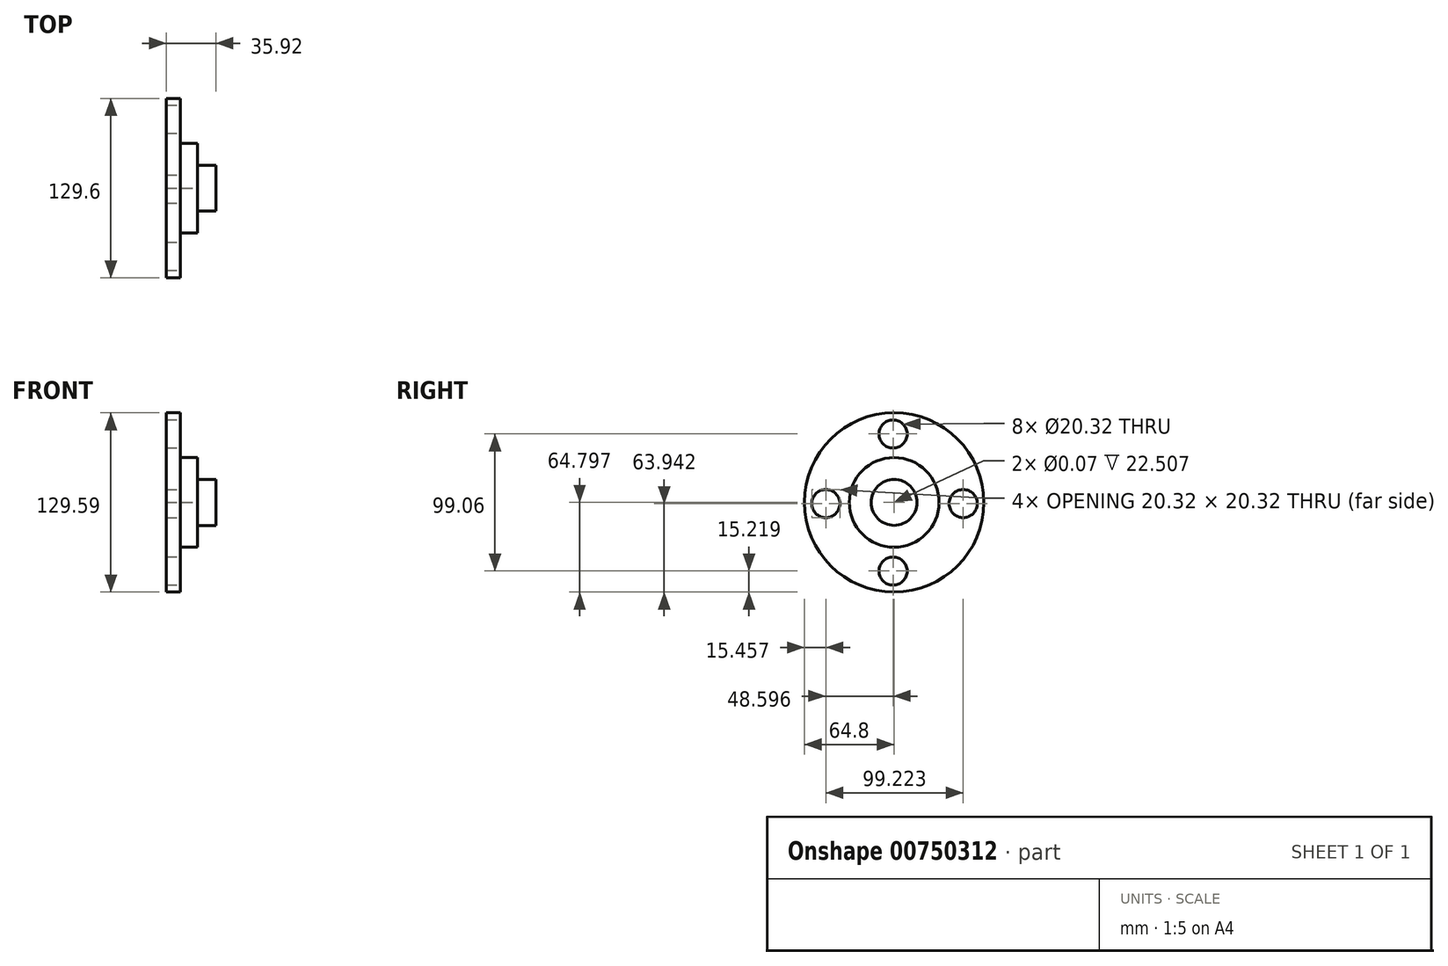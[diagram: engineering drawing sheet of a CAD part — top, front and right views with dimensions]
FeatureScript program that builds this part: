
annotation { "Feature Type Name" : "Feature", "Feature Type Description" : "" }
export const myFeature = defineFeature(function(context is Context, id is Id, definition is map)
    precondition{}
    {
        {
            var Q0;
            Q0=qCreatedBy(makeId("Front.planeOp"),FACE);
            var sketch = newSketch(context, id + "F0", { "sketchPlane" : qUnion([Q0])});
            skLineSegment(sketch, "E0", {"start": v(0, 64.76) * mm, "end": v(0, 0) * mm});
            skLineSegment(sketch, "E1", {"start": v(0, 0) * mm, "end": v(10.3, 0) * mm});
            skLineSegment(sketch, "E2", {"start": v(10.3, 0) * mm, "end": v(10.3, 64.76) * mm});
            skLineSegment(sketch, "E3", {"start": v(10.3, 64.76) * mm, "end": v(0, 64.76) * mm});
            skLineSegment(sketch, "E4", {"start": v(10.3, 0) * mm, "end": v(22.5, 0) * mm});
            skLineSegment(sketch, "E5", {"start": v(22.5, 0) * mm, "end": v(22.5, 32.38) * mm});
            skLineSegment(sketch, "E6", {"start": v(22.5, 32.38) * mm, "end": v(10.3, 32.38) * mm});
            skLineSegment(sketch, "E7", {"start": v(10.3, 32.38) * mm, "end": v(10.3, 0) * mm});
            skLineSegment(sketch, "E8", {"start": v(22.5, 16.55) * mm, "end": v(35.92, 16.55) * mm});
            skLineSegment(sketch, "E9", {"start": v(35.92, 16.55) * mm, "end": v(35.92, -0.03) * mm});
            skLineSegment(sketch, "E10", {"start": v(35.92, -0.03) * mm, "end": v(22.5, -0.03) * mm});
            skLineSegment(sketch, "E11", {"start": v(22.5, -0.03) * mm, "end": v(22.5, 16.55) * mm});
            skSolve(sketch);
        }
        {
            var Q0;
            Q0 = qSketchRegion(id + "F0", true);
            var Q1;
            Q1=sQuery(id+"F0.wireOp",EDGE,"E10");
            revolve(context, id + "F1", {"surfaceOperationType" : NewSurfaceOperationType.NEW, "entities" : qUnion([Q0]), "axis" : qUnion([Q1]), "revolveType" : RevolveType.FULL});
        }
        {
            var Q0;
            Q0=makeQuery(id+"F1.opRevolve","SWEPT_FACE",FACE,{"disambiguationData":[OSD([sQuery(id+"F0.wireOp",EDGE,"E2")])]});
            var sketch = newSketch(context, id + "F2", { "sketchPlane" : qUnion([Q0])});
            skCircle(sketch, "E12", {"center": v(-0.75, 49.45) * mm, "radius": 10.16 * mm});
            skCircle(sketch, "E13", {"center": v(-0.75, -49.61) * mm, "radius": 10.16 * mm});
            skCircle(sketch, "E14", {"center": v(49.88, -0.89) * mm, "radius": 10.16 * mm});
            skCircle(sketch, "E15", {"center": v(-49.34, -0.89) * mm, "radius": 10.16 * mm});
            skSolve(sketch);
        }
        {
            var Q0;
            Q0 = qSketchRegion(id + "F2", true);
            extrude(context, id + "F3", {"entities" : qUnion([Q0]), "operationType" : NewBodyOperationType.REMOVE, "oppositeDirection" : true, "depth" : 25.4 * mm, "offsetDistance" : 25.4 * mm});
        }
    });
